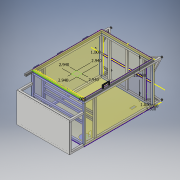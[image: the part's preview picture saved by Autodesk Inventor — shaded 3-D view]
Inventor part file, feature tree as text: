
AUTODESK INVENTOR PART (.ipt)
format: ipt  version: 2019 (Build 230136000, 136)  size: 636,928 bytes
history: native  units: in
note: dims shown in document units (in); Inventor stores cm internally (conversion verified against a paired STEP export)
features: sketch x35, extrude x28, mirror x20, other x9, hole x8, projected_geometry x3, plane x2
ambient origin geometry x8: Origin, YZ Plane, XZ Plane, XY Plane, X Axis, Y Axis, Z Axis, Center Point
bodies: Solid12 (feature_tree), Solid13 (feature_tree), Solid17 (feature_tree), Solid18 (feature_tree)
feature tree (105):
  other  "T-slot rails"
  extrude  "Extrusion1"  Depth=20.0in
  mirror  "Mirror1"
  extrude  "Extrusion2"  Depth=1.0in TaperAngle=0.0deg
  mirror  "Mirror2"
  extrude  "Extrusion3"  Depth=1.0in TaperAngle=0.0deg
  mirror  "Mirror3"
  mirror  "Mirror4"
  plane  "Work Plane1"
  mirror  "Mirror5"
  extrude  "Extrusion4"  TaperAngle=0.0deg  [1 undecoded]
  extrude  "Extrusion5"  Depth=0.5in
  mirror  "Mirror6"
  mirror  "Mirror7"
  extrude  "Extrusion6"  Depth=0.5in
  extrude  "Extrusion7"  Depth=1.0in
  extrude  "Extrusion8"  Depth=0.125in TaperAngle=0.0deg
  mirror  "Mirror8"
  extrude  "Extrusion9"  Depth=0.0625in TaperAngle=0.0deg
  sketch  "Sketch10"  dims[d25=0.0in d26=0.0625in d27=0.0in]
  extrude  "Extrusion12"  TaperAngle=0.0deg  [1 undecoded]
  sketch  "Sketch12"  dims[d28=1.0in d29=0.0in]
  extrude  "Extrusion14"  Depth=1.0in
  extrude  "Extrusion15"  TaperAngle=0.0deg  [1 undecoded]
  mirror  "Mirror10"
  extrude  "Extrusion16"  Depth=1.0in TaperAngle=0.0deg
  extrude  "Extrusion17"  Depth=0.125in TaperAngle=0.0deg
  extrude  "Extrusion18"  TaperAngle=0.0deg  [1 undecoded]
  extrude  "Extrusion19"  Depth=0.5in
  extrude  "Extrusion20"  TaperAngle=0.0deg  [1 undecoded]
  mirror  "Mirror11"
  extrude  "Extrusion23"  Depth=0.5in
  mirror  "Mirror12"
  mirror  "Mirror15"
  extrude  "Extrusion24"  Depth=2.0in
  mirror  "Mirror16"
  mirror  "Mirror17"
  mirror  "Mirror18"
  extrude  "Extrusion25"  TaperAngle=0.0deg  [1 undecoded]
  mirror  "Mirror19"
  mirror  "Mirror20"
  mirror  "Mirror21"
  sketch  "Sketch28"  dims[d64=0.5in d65=2.0in]
  extrude  "Extrusion34"  Depth=3.0in
  mirror  "Mirror24"
  extrude  "Extrusion35"  Depth=3.0in
  mirror  "Mirror25"
  sketch  "Sketch40"  dims[d72=2.0in d73=3.0in]
  extrude  "Extrusion36"  Depth=2.0in
  extrude  "Extrusion37"  Depth=1.0in TaperAngle=0.0deg
  extrude  "Extrusion38"  Depth=20.0in
  hole  "Hole15"  [1 undecoded]
  hole  "Hole16"  [1 undecoded]
  hole  "Hole17"  [1 undecoded]
  hole  "Hole18"  [1 undecoded]
  hole  "Hole22"  [1 undecoded]
  hole  "Hole23"  [1 undecoded]
  hole  "Hole24"  [1 undecoded]
  hole  "Hole25"  [1 undecoded]
  sketch  "Sketch54"  dims[d125=1.0in d126=1.0in]
  sketch  "Sketch55"  dims[d127=1.0in d128=0.0in d129=6.0in]
  extrude  "Extrusion44"  Depth=16.0in
  extrude  "Extrusion45"  TaperAngle=90.0deg  [1 undecoded]
  plane  "Work Plane3"
  sketch  "Sketch58"  dims[d134=1.0in d135=0.0in d162=16.0in d163=90.0deg d164=1.0in d165=1.0in d166=8.0in d167=0.0in d168=1.0in d169=1.0in d170=15.0in d171=0.0in d172=1.0in d173=1.0in d174=29.0in d175=0.0in d176=1.0in d177=1.0in d178=29.0in d179=0.0in d180=17.0in d181=0.125in d182=0.0in d260=5.0in d261=0.38in d262=0.385in d263=0.25in d264=0.5635in d265=0.536in d266=0.8108in d267=5.0in d268=0.38in d269=0.385in d270=0.25in d271=0.5635in d272=0.536in d273=0.8108in d274=5.0in d275=0.38in d276=0.385in d277=0.25in d278=0.5635in d279=3.4375in d280=0.8108in d281=5.1in d282=0.38in d283=0.385in d284=0.25in d285=0.5635in d286=3.4375in d287=0.8108in d316=0.177in d317=0.75in d318=0.37in d319=0.25in d320=90.0deg d321=3.4375in d322=0.8108in d323=0.177in d324=0.75in d325=0.37in d326=0.25in d327=90.0deg d328=3.4375in d329=0.8108in d330=0.177in d331=0.75in d332=0.37in d333=0.25in d334=90.0deg d335=3.4375in d336=0.8108in d337=0.177in d338=0.75in d339=0.37in d340=0.25in d341=90.0deg d342=3.4375in d343=0.8108in d358=1.375in d359=2.63in d360=0.0625in d361=0.0in d362=1.375in d363=2.63in d364=0.0625in d365=0.0in d366=2.94in d367=2.94in d368=2.94in d369=2.94in d99=1.0in d100=1.0in d101=1.0in d102=0.15in d103=0.25in d104=0.375in d105=0.5635in d106=0.75in d107=0.8108in d108=0.0625in d109=0.75in d110=0.375in d211=1.0in d212=1.0in d213=1.0in d214=0.15in d215=0.25in d216=0.375in d217=0.5635in d218=0.75in d219=0.8108in d220=0.0625in d221=0.75in d222=0.375in d288=0.75in d289=0.8108in d290=0.0625in d291=0.75in d292=0.375in d293=0.375in d294=0.5635in d295=0.75in d296=0.8108in d297=0.0625in d298=0.75in d299=0.375in d300=0.8108in d301=0.0625in d302=0.75in d303=0.375in]
  sketch  "Sketch1"  dims[d0=1.0in d1=20.0in]
  sketch  "Sketch2"  dims[d2=14.0in d3=1.0in d4=0.0in]
  other  "More rails"
  sketch  "Sketch3"  dims[d6=1.0in d7=1.0in d8=0.0in]
  other  "Even more rails"
  sketch  "Sketch4"  dims[d9=0.0in d10=0.0in]
  projected_geometry  "Projected Loop1"
  sketch  "Sketch5"  dims[d11=40.0in d12=4.0in d13=0.0in d14=0.0in d15=0.5in]
  other  "Antibration leveling mount"
  sketch  "Sketch6"  dims[d16=0.5in d17=0.5in]
  other  "0.125 in. panel"
  sketch  "Sketch8"  dims[d18=0.8in d19=0.0in d20=1.0in]
  sketch  "Sketch9"  dims[d21=0.2in d22=0.0in d23=0.125in d24=0.0in]
  sketch  "Sketch13"  dims[d31=1.0in d32=0.0in d33=1.0in]
  projected_geometry  "Projected Loop2"
  projected_geometry  "Projected Loop3"
  other  "Door rails"
  sketch  "Sketch14"  dims[d35=0.0in d36=0.0in]
  other  "Door handle"
  sketch  "Sketch16"  dims[d37=1.0in d38=1.0in d39=0.0in]
  other  "Door hinges"
  sketch  "Sketch17"  dims[d42=1.0in d45=0.125in d46=0.0in]
  other  "0.060 in. panel"
  sketch  "Sketch23"  dims[d57=0.0625in d58=0.0in d59=0.5in]
  sketch  "Sketch25"  dims[d60=2.0in d61=0.0in]
  sketch  "Sketch26"  dims[d62=3.0in d63=0.5in]
  sketch  "Sketch38"  dims[d66=0.5in d67=0.0in d68=0.0in]
  sketch  "Sketch39"  dims[d69=0.0625in d70=0.0in d71=3.0in]
  sketch  "Sketch41"  dims[d74=3.0in d75=2.0in]
  sketch  "Sketch42"  dims[d76=0.5in d77=0.0in d78=1.0in d79=0.0in]
  sketch  "Sketch43"  dims[d80=1.0in d81=20.0in]
  sketch  "Sketch48"  dims[d82=1.0in d83=0.0in]
  sketch  "Sketch50"  dims[d90=1.0in d91=20.0in d92=1.0in d94=0.0in d95=1.0in d96=13.5in]
  sketch  "Sketch51"  dims[d97=3.5in d98=32.0in]
  sketch  "Sketch52"  dims[d120=1.0in d121=1.0in]
  sketch  "Sketch53"  dims[d122=8.0in d123=0.0in d124=6.0in]
  sketch  "Sketch56"  dims[d130=1.0in d131=90.0deg]
  sketch  "Sketch57"  dims[d132=1.0in d133=1.0in]
  extrude  "Extrusion22"  Depth=1.0in
  sketch  "Sketch19"  dims[d49=1.0in d50=0.0in d56=0.0in]
note: 15 required parameter values undecoded (feature->parameter linkage not recoverable at this tier; creation-order binding heuristic only, values carry confidence <= 0.55)
